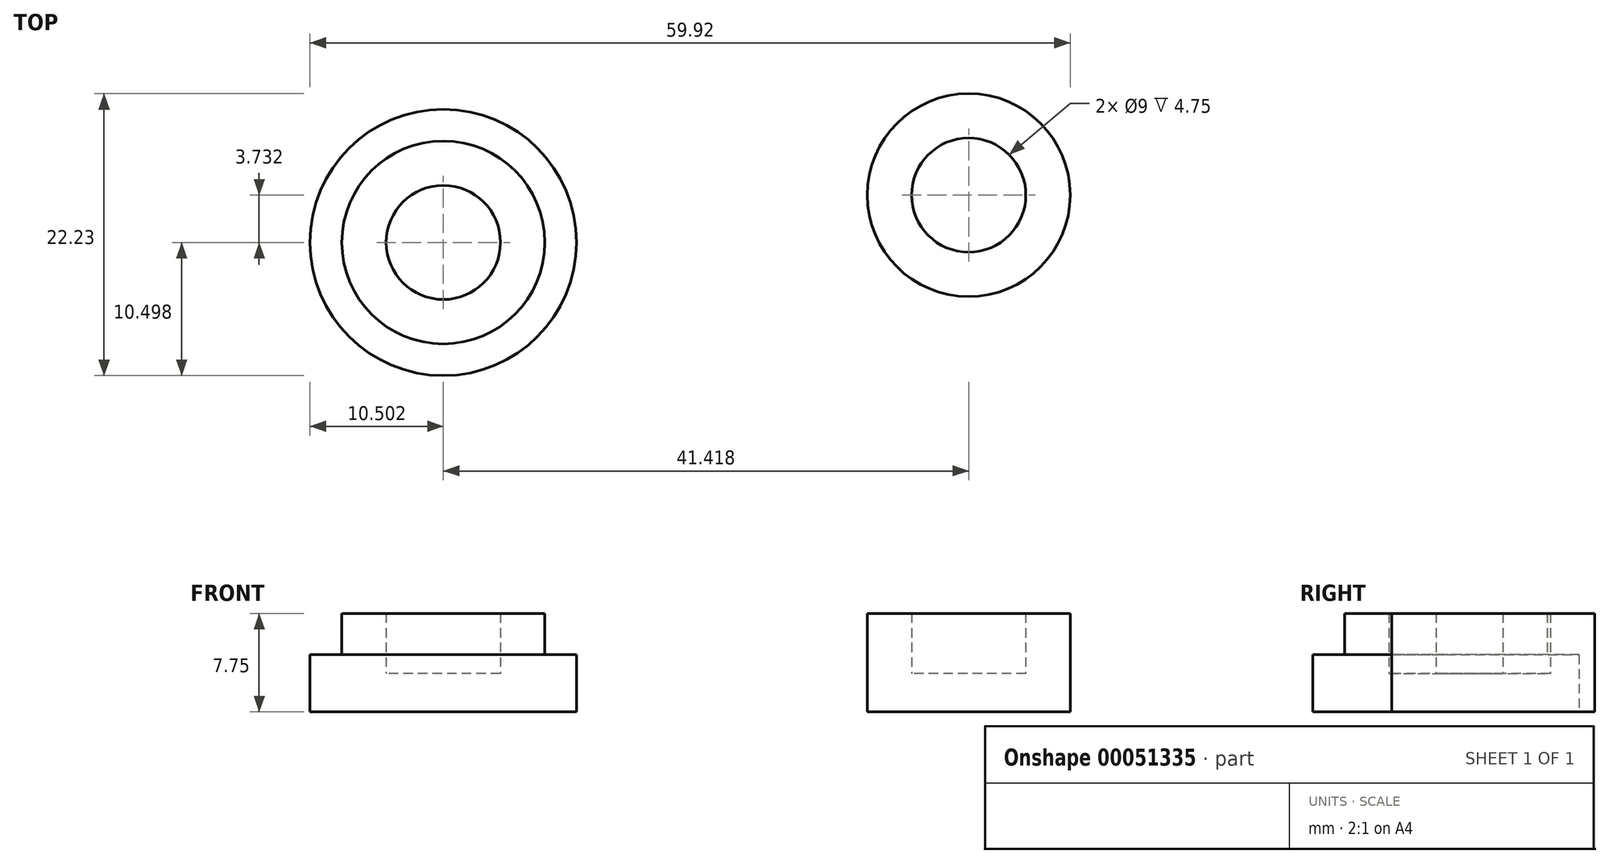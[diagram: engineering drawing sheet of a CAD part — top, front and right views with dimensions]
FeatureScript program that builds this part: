
annotation { "Feature Type Name" : "Feature", "Feature Type Description" : "" }
export const myFeature = defineFeature(function(context is Context, id is Id, definition is map)
    precondition{}
    {
        {
            var Q0;
            Q0=qCreatedBy(makeId("Top.planeOp"),FACE);
            var sketch = newSketch(context, id + "F0", { "sketchPlane" : qUnion([Q0])});
            skCircle(sketch, "E0", {"center": v(0, 0) * mm, "radius": 4.5 * mm});
            skCircle(sketch, "E1", {"center": v(0, 0) * mm, "radius": 8 * mm});
            skCircle(sketch, "E2", {"center": v(-41.42, -3.73) * mm, "radius": 4.5 * mm});
            skCircle(sketch, "E3", {"center": v(-41.42, -3.73) * mm, "radius": 8 * mm});
            skCircle(sketch, "E4", {"center": v(-41.42, -3.73) * mm, "radius": 10.5 * mm});
            skSolve(sketch);
        }
        {
            var Q0;
            Q0=makeQuery(id+"F0.imprint","IMPRINT",FACE,{"disambiguationData":[TD([[makeQuery(id+"F0.imprint","IMPRINT",EDGE,{"derivedFrom":sQuery(id+"F0.wireOp",EDGE,"E0")}),-1.0]])]});
            var Q1;
            Q1=makeQuery(id+"F0.imprint","IMPRINT",FACE,{"disambiguationData":[TD([[makeQuery(id+"F0.imprint","IMPRINT",EDGE,{"derivedFrom":sQuery(id+"F0.wireOp",EDGE,"E2")}),-1.0]])]});
            extrude(context, id + "F1", {"entities" : qUnion([Q0, Q1]), "depth" : 7.75 * mm});
        }
        {
            var Q0;
            Q0=makeQuery(id+"F0.imprint","IMPRINT",FACE,{"disambiguationData":[TD([[makeQuery(id+"F0.imprint","IMPRINT",EDGE,{"derivedFrom":sQuery(id+"F0.wireOp",EDGE,"E0")}),1.0]])]});
            var Q1;
            Q1=makeQuery(id+"F0.imprint","IMPRINT",FACE,{"disambiguationData":[TD([[makeQuery(id+"F0.imprint","IMPRINT",EDGE,{"derivedFrom":sQuery(id+"F0.wireOp",EDGE,"E2")}),1.0]])]});
            extrude(context, id + "F2", {"entities" : qUnion([Q0, Q1]), "operationType" : NewBodyOperationType.ADD, "depth" : 3 * mm});
        }
        {
            var Q0;
            Q0=makeQuery(id+"F0.imprint","IMPRINT",FACE,{"disambiguationData":[TD([[makeQuery(id+"F0.imprint","IMPRINT",EDGE,{"derivedFrom":sQuery(id+"F0.wireOp",EDGE,"E3")}),-1.0]])]});
            extrude(context, id + "F3", {"entities" : qUnion([Q0]), "operationType" : NewBodyOperationType.ADD, "depth" : 4.5 * mm});
        }
    });
